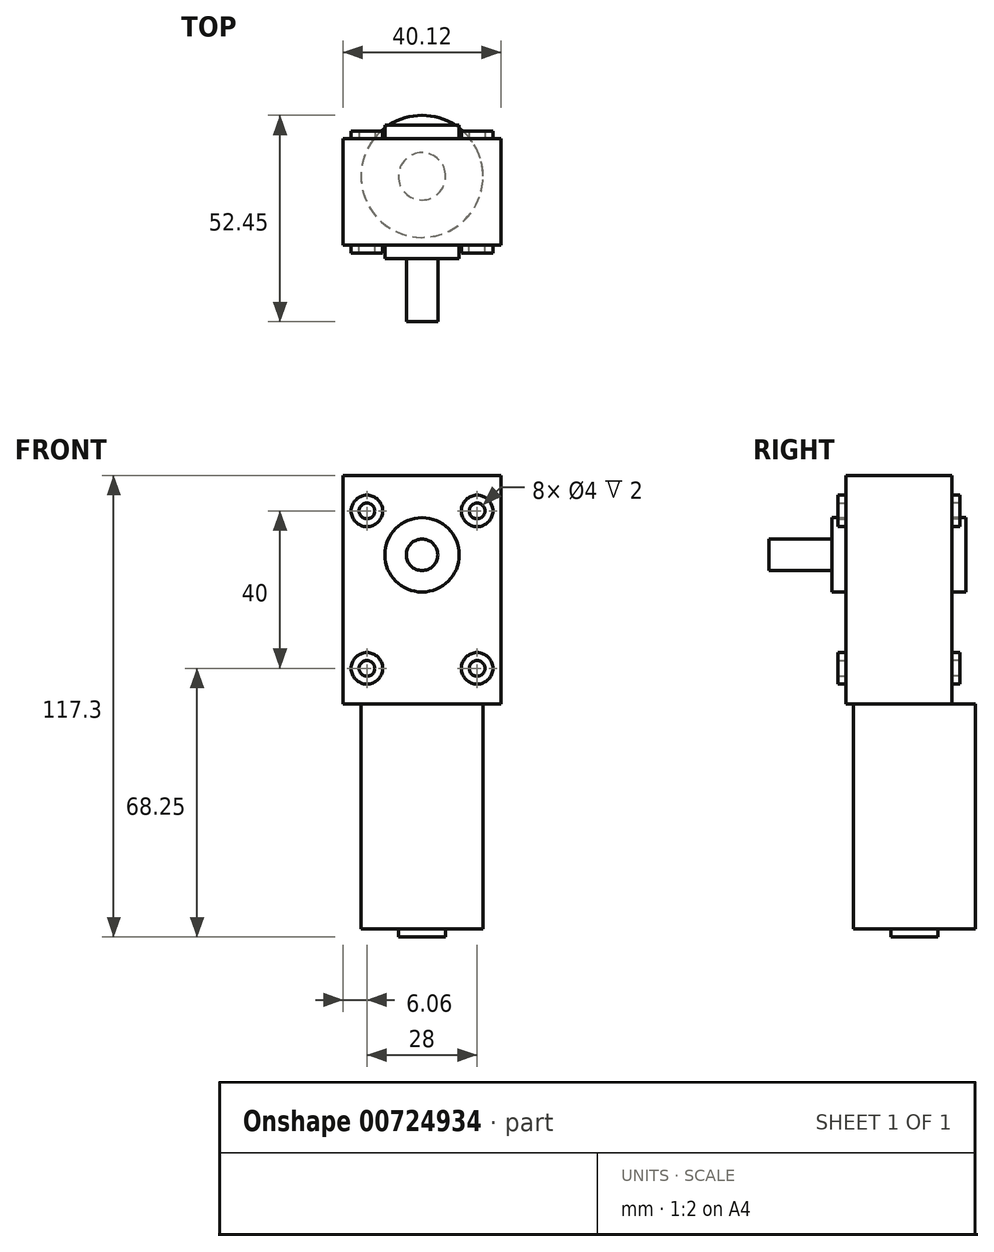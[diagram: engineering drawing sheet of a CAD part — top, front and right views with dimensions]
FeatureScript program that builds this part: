
annotation { "Feature Type Name" : "Feature", "Feature Type Description" : "" }
export const myFeature = defineFeature(function(context is Context, id is Id, definition is map)
    precondition{}
    {
        {
            var Q0;
            Q0=qCreatedBy(makeId("Top.planeOp"),FACE);
            var sketch = newSketch(context, id + "F0", { "sketchPlane" : qUnion([Q0])});
            skCircle(sketch, "E0", {"center": v(0, 0) * mm, "radius": 15.5 * mm});
            skSolve(sketch);
        }
        {
            var Q0;
            Q0=makeQuery(id+"F0.imprint","IMPRINT",FACE,{"disambiguationData":[TD([[makeQuery(id+"F0.imprint","IMPRINT",EDGE,{"derivedFrom":sQuery(id+"F0.wireOp",EDGE,"E0")}),1.0]])]});
            extrude(context, id + "F1", {"entities" : qUnion([Q0]), "depth" : 57.2 * mm, "offsetDistance" : 25 * mm});
        }
        {
            var Q0;
            Q0=makeQuery(id+"F1.opExtrude","CAP_FACE",FACE,{"disambiguationData":[OSD([sQuery(id+"F0.wireOp",EDGE,"E0")])],"isStart":false});
            var sketch = newSketch(context, id + "F2", { "sketchPlane" : qUnion([Q0])});
            skLineSegment(sketch, "E1.bottom", {"start": v(-20.06, 9.55) * mm, "end": v(20.06, 9.55) * mm});
            skLineSegment(sketch, "E1.top", {"start": v(-20.06, -17.45) * mm, "end": v(20.06, -17.45) * mm});
            skLineSegment(sketch, "E1.left", {"start": v(-20.06, 9.55) * mm, "end": v(-20.06, -17.45) * mm});
            skLineSegment(sketch, "E1.right", {"start": v(20.06, 9.55) * mm, "end": v(20.06, -17.45) * mm});
            skSolve(sketch);
        }
        {
            var Q0;
            Q0=makeQuery(id+"F2.imprint","IMPRINT",FACE,{"disambiguationData":[TD([[makeQuery(id+"F2.imprint","IMPRINT",EDGE,{"derivedFrom":sQuery(id+"F2.wireOp",EDGE,"E1.top")}),1.0]])]});
            var Q1;
            {var subQ0=sQuery(id+"F2.wireOp",EDGE,"E1.bottom");var subQ1=makeQuery(id+"F1.opExtrude","CAP_EDGE",EDGE,{"disambiguationData":[OSD([sQuery(id+"F0.wireOp",EDGE,"E0")])],"isStart":false});var subQ2=makeQuery(id+"F2.imprint","INTERSECT",VERTEX,{"disambiguationData":[OD(0.0)],"derivedFrom":[subQ1,subQ0]});Q1=makeQuery(id+"F2.imprint","IMPRINT",FACE,{"disambiguationData":[TD([[makeQuery(id+"F2.imprint","IMPRINT",EDGE,{"disambiguationData":[TD([[subQ2,-1.0]])],"derivedFrom":subQ0}),-1.0]])]});}
            extrude(context, id + "F3", {"entities" : qUnion([Q0, Q1]), "operationType" : NewBodyOperationType.ADD, "depth" : 58.1 * mm, "offsetDistance" : 25 * mm});
        }
        {
            var Q0;
            Q0=makeQuery(id+"F3.opExtrude","SWEPT_FACE",FACE,{"disambiguationData":[OSD([sQuery(id+"F2.wireOp",EDGE,"E1.top")])]});
            var sketch = newSketch(context, id + "F4", { "sketchPlane" : qUnion([Q0])});
            skCircle(sketch, "E2", {"center": v(0, 95.1) * mm, "radius": 9.45 * mm});
            skSolve(sketch);
        }
        {
            var Q0;
            Q0=makeQuery(id+"F4.imprint","IMPRINT",FACE,{"disambiguationData":[TD([[makeQuery(id+"F4.imprint","IMPRINT",EDGE,{"derivedFrom":sQuery(id+"F4.wireOp",EDGE,"E2")}),1.0]])]});
            extrude(context, id + "F5", {"entities" : qUnion([Q0]), "operationType" : NewBodyOperationType.ADD, "depth" : 3.5 * mm, "offsetDistance" : 25 * mm});
        }
        {
            var Q0;
            Q0=makeQuery(id+"F5.opExtrude","CAP_FACE",FACE,{"disambiguationData":[OSD([sQuery(id+"F4.wireOp",EDGE,"E2")])],"isStart":false});
            extrude(context, id + "F6", {"entities" : qUnion([Q0]), "operationType" : NewBodyOperationType.ADD, "oppositeDirection" : true, "depth" : 34 * mm, "offsetDistance" : 25 * mm});
        }
        {
            var Q0;
            Q0=makeQuery(id+"F5.opExtrude","CAP_FACE",FACE,{"disambiguationData":[OSD([sQuery(id+"F4.wireOp",EDGE,"E2")])],"isStart":false});
            var sketch = newSketch(context, id + "F7", { "sketchPlane" : qUnion([Q0])});
            skCircle(sketch, "E3", {"center": v(0, 95.1) * mm, "radius": 4 * mm});
            skSolve(sketch);
        }
        {
            var Q0;
            Q0=makeQuery(id+"F7.imprint","IMPRINT",FACE,{"disambiguationData":[TD([[makeQuery(id+"F7.imprint","IMPRINT",EDGE,{"derivedFrom":sQuery(id+"F7.wireOp",EDGE,"E3")}),1.0]])]});
            extrude(context, id + "F8", {"entities" : qUnion([Q0]), "operationType" : NewBodyOperationType.ADD, "depth" : (50 - 34) * mm, "offsetDistance" : 25 * mm});
        }
        {
            var Q0;
            Q0=makeQuery(id+"F3.opExtrude","SWEPT_FACE",FACE,{"disambiguationData":[OSD([sQuery(id+"F2.wireOp",EDGE,"E1.top")])]});
            var sketch = newSketch(context, id + "F9", { "sketchPlane" : qUnion([Q0])});
            skLineSegment(sketch, "E4.bottom", {"start": v(-14, 106.25) * mm, "end": v(14, 106.25) * mm, "construction": true});
            skLineSegment(sketch, "E4.top", {"start": v(-14, 66.25) * mm, "end": v(14, 66.25) * mm, "construction": true});
            skLineSegment(sketch, "E4.left", {"start": v(-14, 106.25) * mm, "end": v(-14, 66.25) * mm, "construction": true});
            skLineSegment(sketch, "E4.right", {"start": v(14, 106.25) * mm, "end": v(14, 66.25) * mm, "construction": true});
            skCircle(sketch, "E5", {"center": v(14, 106.25) * mm, "radius": 4 * mm});
            skCircle(sketch, "E6", {"center": v(-14, 106.25) * mm, "radius": 4 * mm});
            skCircle(sketch, "E7", {"center": v(14, 66.25) * mm, "radius": 4 * mm});
            skCircle(sketch, "E8", {"center": v(-14, 66.25) * mm, "radius": 4 * mm});
            skCircle(sketch, "E9", {"center": v(-14, 106.25) * mm, "radius": 2 * mm});
            skCircle(sketch, "E10", {"center": v(14, 106.25) * mm, "radius": 2 * mm});
            skCircle(sketch, "E11", {"center": v(14, 66.25) * mm, "radius": 2 * mm});
            skCircle(sketch, "E12", {"center": v(-14, 66.25) * mm, "radius": 2 * mm});
            skSolve(sketch);
        }
        {
            var Q0;
            Q0=makeQuery(id+"F9.imprint","IMPRINT",FACE,{"disambiguationData":[TD([[makeQuery(id+"F9.imprint","IMPRINT",EDGE,{"derivedFrom":sQuery(id+"F9.wireOp",EDGE,"E5")}),1.0]])]});
            var Q1;
            Q1=makeQuery(id+"F9.imprint","IMPRINT",FACE,{"disambiguationData":[TD([[makeQuery(id+"F9.imprint","IMPRINT",EDGE,{"derivedFrom":sQuery(id+"F9.wireOp",EDGE,"E6")}),1.0]])]});
            var Q2;
            Q2=makeQuery(id+"F9.imprint","IMPRINT",FACE,{"disambiguationData":[TD([[makeQuery(id+"F9.imprint","IMPRINT",EDGE,{"derivedFrom":sQuery(id+"F9.wireOp",EDGE,"E7")}),1.0]])]});
            var Q3;
            Q3=makeQuery(id+"F9.imprint","IMPRINT",FACE,{"disambiguationData":[TD([[makeQuery(id+"F9.imprint","IMPRINT",EDGE,{"derivedFrom":sQuery(id+"F9.wireOp",EDGE,"E8")}),1.0]])]});
            extrude(context, id + "F10", {"entities" : qUnion([Q0, Q1, Q2, Q3]), "operationType" : NewBodyOperationType.ADD, "depth" : 2 * mm, "offsetDistance" : 25 * mm});
        }
        {
            var Q0;
            Q0 = qSketchRegion(id + "F9", true);
            extrude(context, id + "F11", {"entities" : qUnion([Q0]), "operationType" : NewBodyOperationType.ADD, "oppositeDirection" : true, "depth" : 29 * mm, "offsetDistance" : 25 * mm});
        }
        {
            var Q0;
            Q0=makeQuery(id+"F1.opExtrude","CAP_FACE",FACE,{"disambiguationData":[OSD([sQuery(id+"F0.wireOp",EDGE,"E0")])],"isStart":true});
            var sketch = newSketch(context, id + "F12", { "sketchPlane" : qUnion([Q0])});
            skCircle(sketch, "E13", {"center": v(0, 0) * mm, "radius": 6 * mm});
            skSolve(sketch);
        }
        {
            var Q0;
            Q0=makeQuery(id+"F12.imprint","IMPRINT",FACE,{"disambiguationData":[TD([[makeQuery(id+"F12.imprint","IMPRINT",EDGE,{"derivedFrom":sQuery(id+"F12.wireOp",EDGE,"E13")}),1.0]])]});
            extrude(context, id + "F13", {"entities" : qUnion([Q0]), "operationType" : NewBodyOperationType.ADD, "depth" : 2 * mm, "offsetDistance" : 25 * mm});
        }
    });
